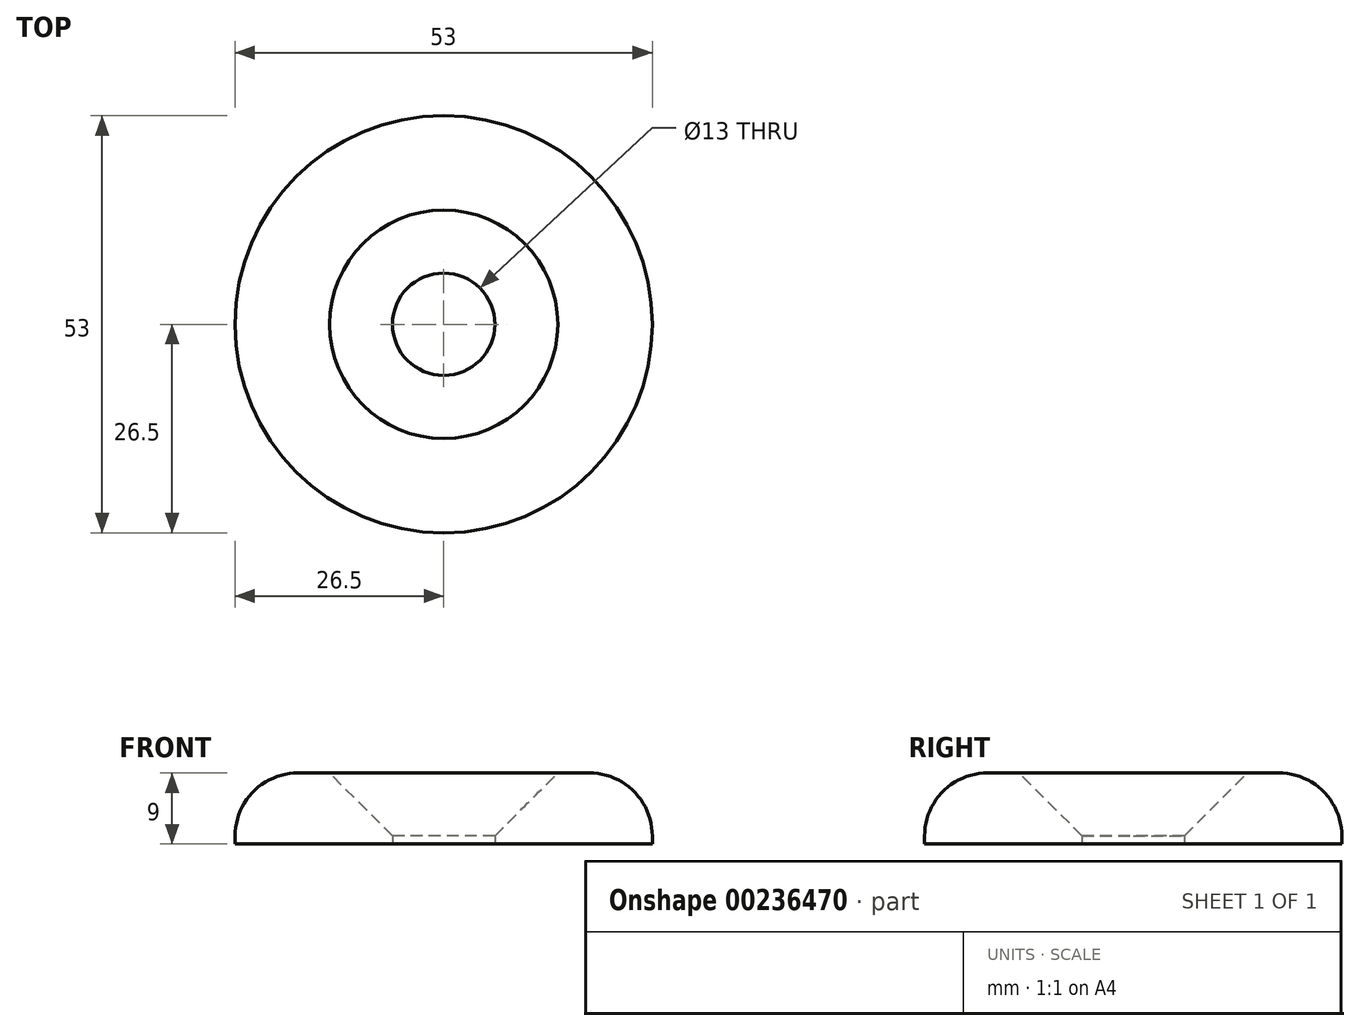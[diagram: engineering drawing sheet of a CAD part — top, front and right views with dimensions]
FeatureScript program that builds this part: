
annotation { "Feature Type Name" : "Feature", "Feature Type Description" : "" }
export const myFeature = defineFeature(function(context is Context, id is Id, definition is map)
    precondition{}
    {
        {
            var Q0;
            Q0=qCreatedBy(makeId("Top.planeOp"),FACE);
            var sketch = newSketch(context, id + "F0", { "sketchPlane" : qUnion([Q0])});
            skCircle(sketch, "E0", {"center": v(0, 0) * mm, "radius": 6.5 * mm});
            skCircle(sketch, "E1", {"center": v(0, 0) * mm, "radius": 26.5 * mm});
            skSolve(sketch);
        }
        {
            var Q0;
            Q0=makeQuery(id+"F0.imprint","IMPRINT",FACE,{"disambiguationData":[TD([[makeQuery(id+"F0.imprint","IMPRINT",EDGE,{"derivedFrom":sQuery(id+"F0.wireOp",EDGE,"E0")}),-1.0]])]});
            extrude(context, id + "F1", {"entities" : qUnion([Q0]), "depth" : 9 * mm, "offsetDistance" : 25 * mm});
        }
        {
            var Q0;
            Q0=makeQuery(id+"F1.opExtrude","CAP_EDGE",EDGE,{"disambiguationData":[OSD([sQuery(id+"F0.wireOp",EDGE,"E1")])],"isStart":false});
            fillet(context, id + "F2", {"entities" : qUnion([Q0]), "tangentPropagation" : true, "radius" : 8 * mm, "defaultsChanged" : true, "vertexSettings" : [], "allowEdgeOverflow" : false});
        }
        {
            var Q0;
            Q0=makeQuery(id+"F1.opExtrude","CAP_EDGE",EDGE,{"disambiguationData":[OSD([sQuery(id+"F0.wireOp",EDGE,"E0")])],"isStart":false});
            chamfer(context, id + "F3", {"entities" : qUnion([Q0]), "width" : 8 * mm, "tangentPropagation" : true});
        }
    });
